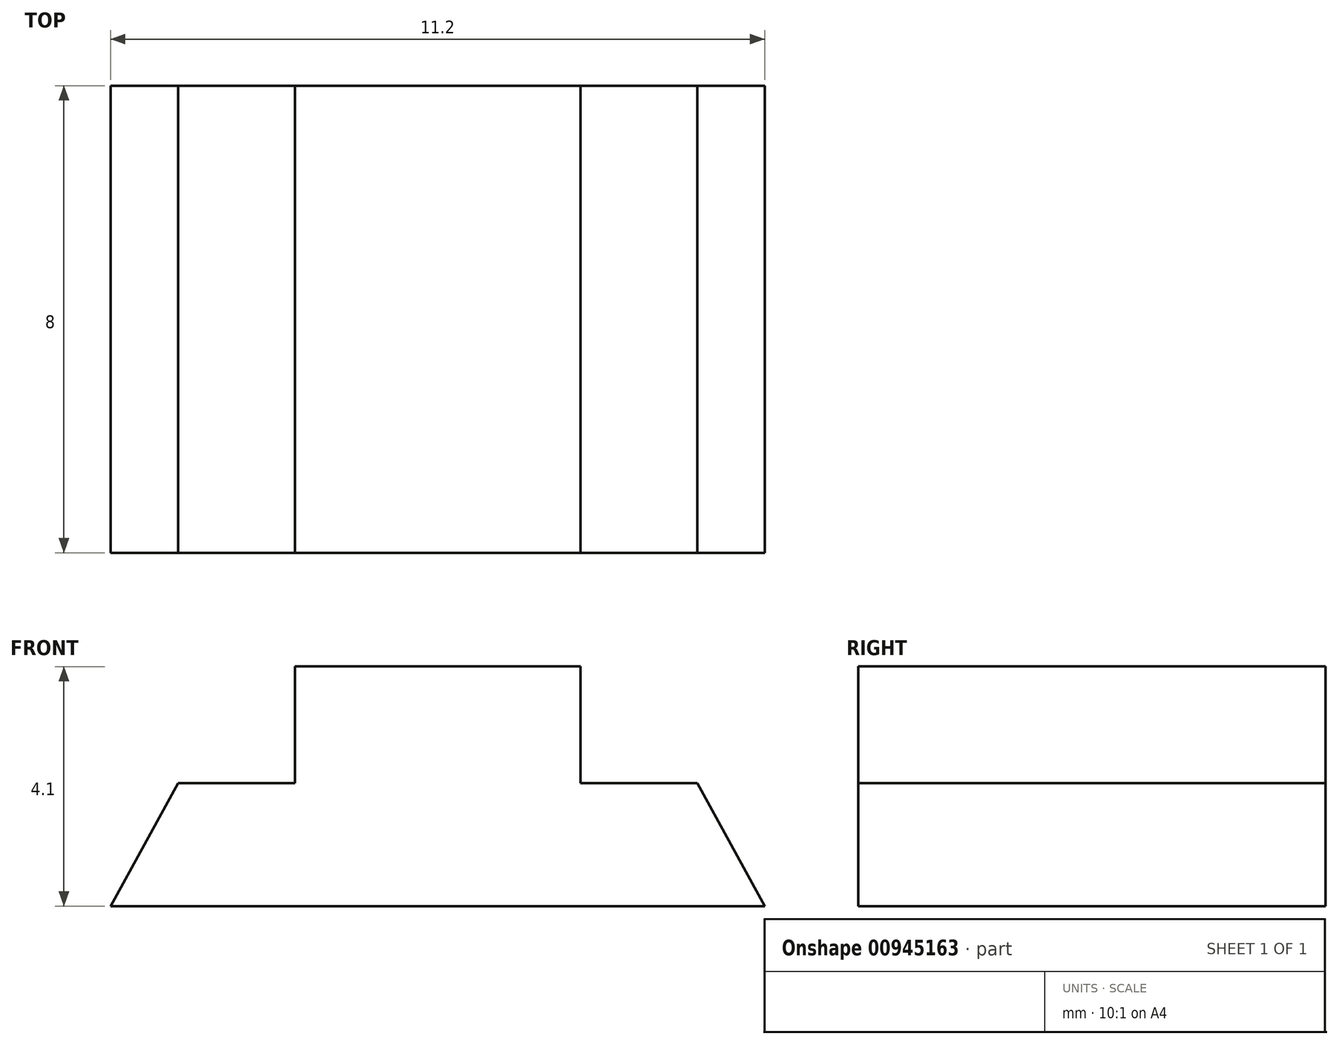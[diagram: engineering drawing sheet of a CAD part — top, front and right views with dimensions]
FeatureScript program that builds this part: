
annotation { "Feature Type Name" : "Feature", "Feature Type Description" : "" }
export const myFeature = defineFeature(function(context is Context, id is Id, definition is map)
    precondition{}
    {
        {
            var Q0;
            Q0=qCreatedBy(makeId("Front.planeOp"),FACE);
            var sketch = newSketch(context, id + "F0", { "sketchPlane" : qUnion([Q0])});
            skLineSegment(sketch, "E0", {"start": v(0, 0) * mm, "end": v(-6, 0) * mm, "construction": true});
            skLineSegment(sketch, "E1", {"start": v(0, 0) * mm, "end": v(0, 2.4) * mm, "construction": true});
            skLineSegment(sketch, "E2", {"start": v(0, 2.4) * mm, "end": v(-4.68, 2.4) * mm, "construction": true});
            skLineSegment(sketch, "E3", {"start": v(-4.68, 2.4) * mm, "end": v(-6, 0) * mm, "construction": true});
            skLineSegment(sketch, "E4.MirrorCS", {"start": v(4.68, 2.4) * mm, "end": v(6, 0) * mm, "construction": true});
            skLineSegment(sketch, "E5.MirrorCS", {"start": v(0, 2.4) * mm, "end": v(4.68, 2.4) * mm, "construction": true});
            skLineSegment(sketch, "E6.MirrorCS", {"start": v(0, 0) * mm, "end": v(6, 0) * mm, "construction": true});
            skLineSegment(sketch, "E7", {"start": v(0, 0) * mm, "end": v(-5.6, 0) * mm});
            skLineSegment(sketch, "E8", {"start": v(-5.6, 0) * mm, "end": v(-4.45, 2.1) * mm});
            skLineSegment(sketch, "E9", {"start": v(-4.45, 2.1) * mm, "end": v(-2.45, 2.1) * mm});
            skLineSegment(sketch, "E10", {"start": v(-2.45, 2.1) * mm, "end": v(-2.45, 4.1) * mm});
            skLineSegment(sketch, "E11", {"start": v(-2.45, 4.1) * mm, "end": v(0, 4.1) * mm});
            skLineSegment(sketch, "E12.MirrorCS", {"start": v(2.45, 4.1) * mm, "end": v(0, 4.1) * mm});
            skLineSegment(sketch, "E13.MirrorCS", {"start": v(2.45, 2.1) * mm, "end": v(2.45, 4.1) * mm});
            skLineSegment(sketch, "E14.MirrorCS", {"start": v(4.45, 2.1) * mm, "end": v(2.45, 2.1) * mm});
            skLineSegment(sketch, "E15.MirrorCS", {"start": v(5.6, 0) * mm, "end": v(4.45, 2.1) * mm});
            skLineSegment(sketch, "E16", {"start": v(0, 0) * mm, "end": v(5.6, 0) * mm});
            skSolve(sketch);
        }
        {
            var Q0;
            Q0=qSketchRegion(id+"F0",true);
            extrude(context, id + "F1", {"entities" : qUnion([Q0]), "depth" : 8 * mm, "offsetDistance" : 25 * mm});
        }
    });
